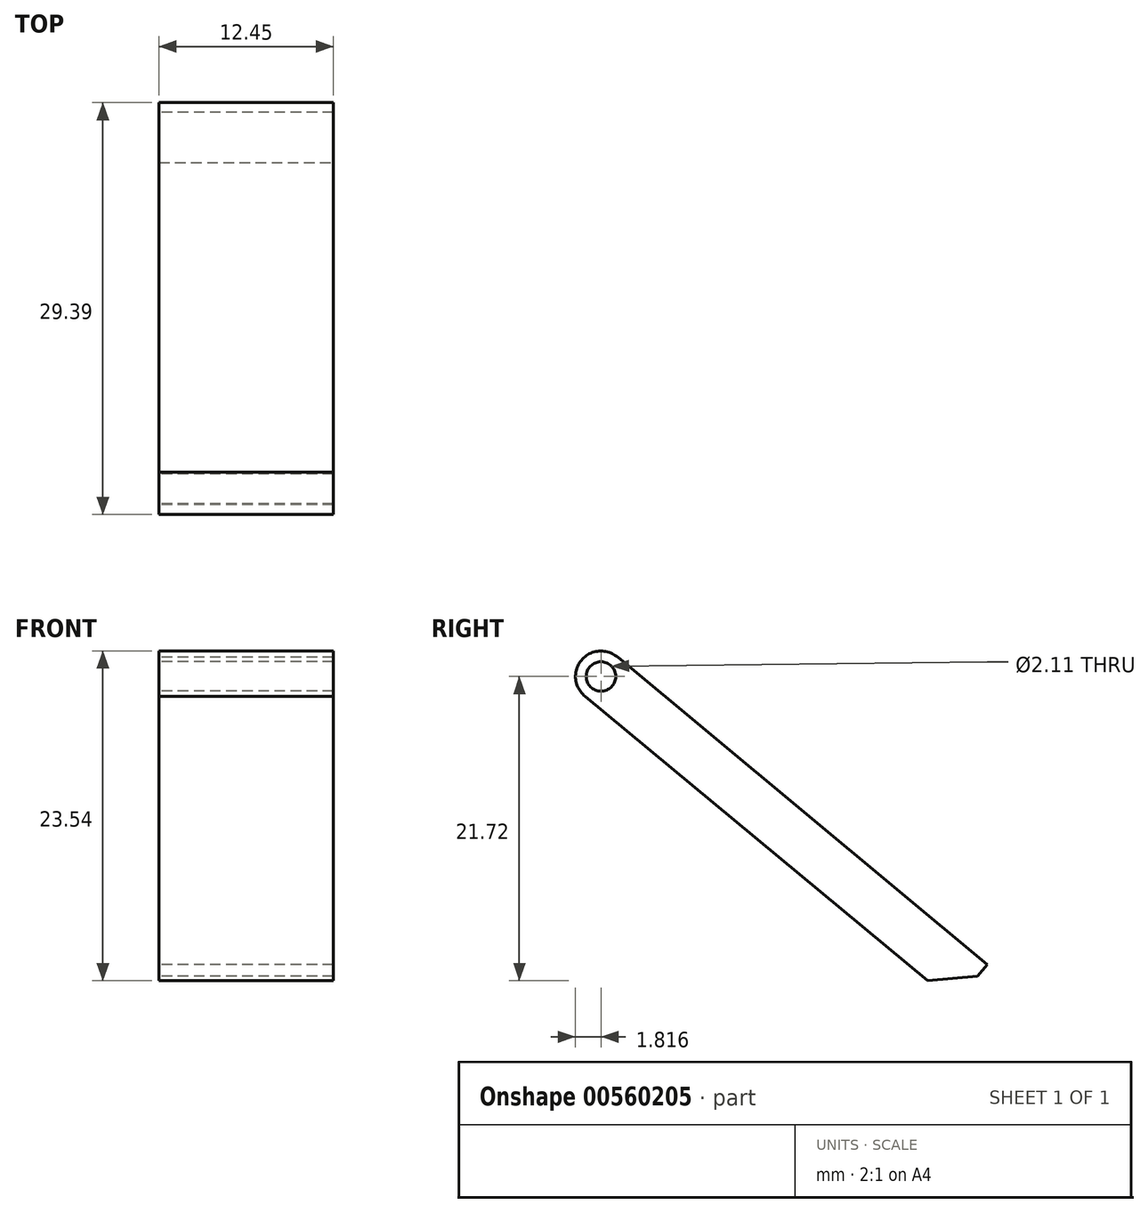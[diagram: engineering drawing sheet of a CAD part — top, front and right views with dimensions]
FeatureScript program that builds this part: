
annotation { "Feature Type Name" : "Feature", "Feature Type Description" : "" }
export const myFeature = defineFeature(function(context is Context, id is Id, definition is map)
    precondition{}
    {
        {
            var Q0;
            Q0=qCreatedBy(makeId("Right.planeOp"),FACE);
            var sketch = newSketch(context, id + "F0", { "sketchPlane" : qUnion([Q0])});
            skLineSegment(sketch, "E0.0", {"start": v(-9.57, -12.13) * mm, "end": v(-35.94, 9.78) * mm});
            skArc(sketch, "E1.MirrorC", {"start": v(-35.94, 9.78) * mm, "mid": v(-36.22, 12.37) * mm, "end": v(-33.62, 12.57) * mm});
            skPoint(sketch, "E2.start.orphan", {"position": v(-22.75, -1.18) * mm});
            skCircle(sketch, "E3.0", {"center": v(-34.82, 11.2) * mm, "radius": 1.05 * mm});
            skPoint(sketch, "E4.orphan", {"position": v(-35.94, 9.78) * mm});
            skLineSegment(sketch, "E5.MirrorCS", {"start": v(-7.25, -9.34) * mm, "end": v(-33.62, 12.57) * mm});
            skLineSegment(sketch, "E6", {"start": v(-9.57, -12.13) * mm, "end": v(-7.25, -9.34) * mm});
            skSolve(sketch);
        }
        {
            var Q0;
            Q0=makeQuery(id+"F0.imprint","IMPRINT",FACE,{"disambiguationData":[TD([[makeQuery(id+"F0.imprint","IMPRINT",EDGE,{"derivedFrom":sQuery(id+"F0.wireOp",EDGE,"E0.0")}),-1.0]])]});
            extrude(context, id + "F1", {"entities" : qUnion([Q0]), "depth" : 12.45 * mm, "offsetDistance" : 25.4 * mm});
        }
        {
            var Q0;
            Q0=makeQuery(id+"F1.opExtrude","SWEPT_EDGE",EDGE,{"disambiguationData":[OSD([sQuery(id+"F0.wireOp",EDGE,"E0.0"),sQuery(id+"F0.wireOp",EDGE,"E6")])]});
            chamfer(context, id + "F2", {"entities" : qUnion([Q0]), "width" : 2.54 * mm, "tangentPropagation" : true});
        }
    });
